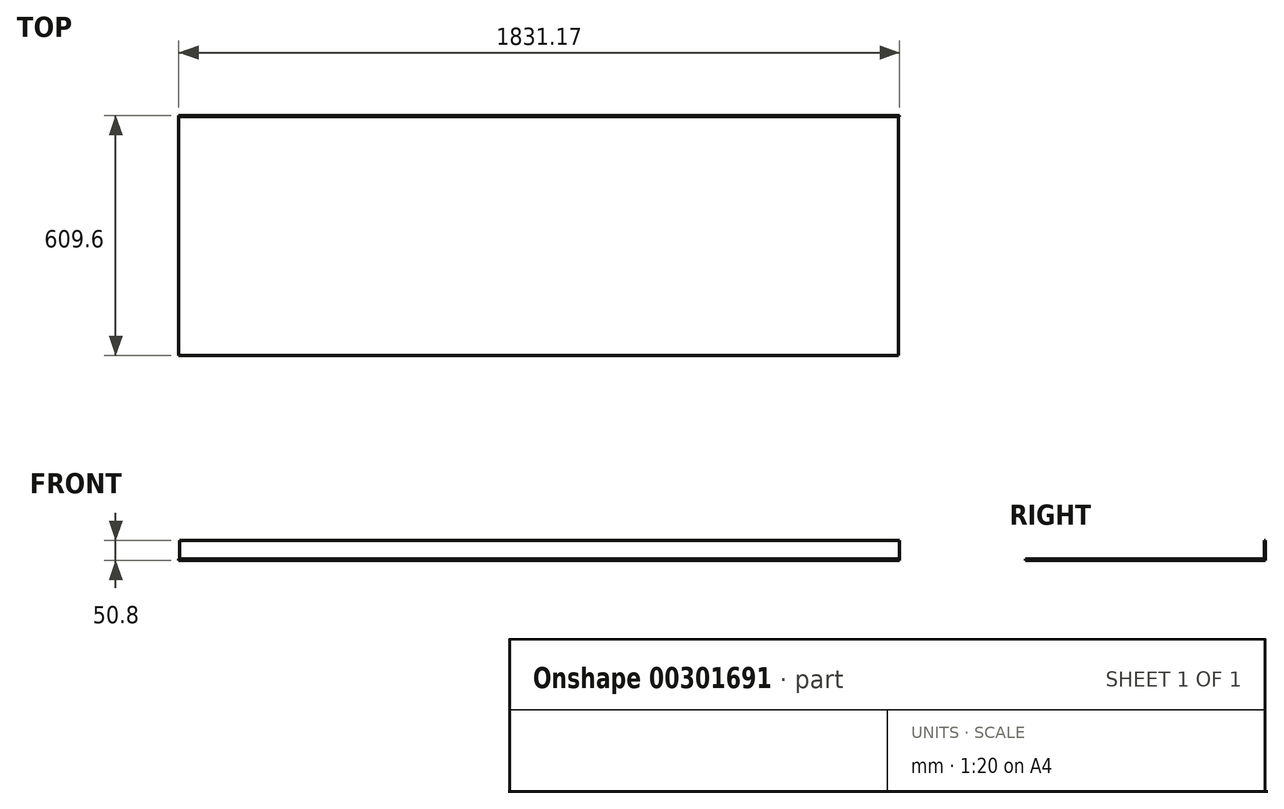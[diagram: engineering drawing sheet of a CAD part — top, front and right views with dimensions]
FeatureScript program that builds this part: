
annotation { "Feature Type Name" : "Feature", "Feature Type Description" : "" }
export const myFeature = defineFeature(function(context is Context, id is Id, definition is map)
    precondition{}
    {
        {
            var Q0;
            Q0=qCreatedBy(makeId("Top.planeOp"),FACE);
            var sketch = newSketch(context, id + "F0", { "sketchPlane" : qUnion([Q0])});
            skLineSegment(sketch, "E0.bottom", {"start": v(-860.21, 0) * mm, "end": v(968.59, 0) * mm});
            skLineSegment(sketch, "E0.top", {"start": v(-860.21, -609.6) * mm, "end": v(968.59, -609.6) * mm});
            skLineSegment(sketch, "E0.left", {"start": v(-860.21, 0) * mm, "end": v(-860.21, -609.6) * mm});
            skLineSegment(sketch, "E0.right", {"start": v(968.59, 0) * mm, "end": v(968.59, -609.6) * mm});
            skSolve(sketch);
        }
        {
            var Q0;
            Q0 = qSketchRegion(id + "F0", true);
            extrude(context, id + "F1", {"entities" : qUnion([Q0]), "depth" : 3.17 * mm});
        }
        {
            var Q0;
            Q0=qCreatedBy(makeId("Front.planeOp"),FACE);
            var sketch = newSketch(context, id + "F2", { "sketchPlane" : qUnion([Q0])});
            skLineSegment(sketch, "E1.bottom", {"start": v(-857.84, 0) * mm, "end": v(970.96, 0) * mm});
            skLineSegment(sketch, "E1.top", {"start": v(-857.84, 50.8) * mm, "end": v(970.96, 50.8) * mm});
            skLineSegment(sketch, "E1.left", {"start": v(-857.84, 0) * mm, "end": v(-857.84, 50.8) * mm});
            skLineSegment(sketch, "E1.right", {"start": v(970.96, 0) * mm, "end": v(970.96, 50.8) * mm});
            skSolve(sketch);
        }
        {
            var Q0;
            Q0 = qSketchRegion(id + "F2", true);
            extrude(context, id + "F3", {"entities" : qUnion([Q0]), "operationType" : NewBodyOperationType.ADD, "depth" : 3.17 * mm});
        }
    });
